# Revit family: BC_Hitachi_CH-Box-6.0-10.0_LOD400
name_source: partatom
category: Equipement de génie climatique
revit_build: Autodesk Revit 2016 (Build: 20150220_1215(x64)
units: mm (PartAtom-declared; Revit-internal decimal feet)

## family parameters
Basée sur le plan de construction = Non
Cote de connecteur circulaire = Utiliser le diamètre
Couper avec des vides une fois chargée = Non
Numéro OmniClass = 23.75.50.00
Partagée = Non
Point de calcul de pièce = Non
Titre OmniClass = Energy Treatment
Toujours verticalement = Oui
Type d'élément = Normal

## types (2) — shared parameters
Color = Neutral white (4.56Y8.85/0.38)
Description = Energy recovery box
Electrical Box = 63 mm
Fabricant = HITACHI
Frequency = 50 Hz
Gas HP distance = 20 mm  [stored 0.0656168 ft]
Gas High pressure Height = 94 mm
Gas low pressure Height = 40 mm
Input = 20 W
Mass = 7.00 kg
Modèle = Indoor unit CH Box CH-N2
Nominal Voltage = 240 V
Number of Poles = 1
Operation and service space = Oui
Overall Depth = 191 mm  [stored 0.62664 ft]
Overall Height = 301 mm
Overall Width = 214 mm  [stored 0.7021 ft]
Power Supply = 240 V
Refrigerant = R410A
Refrigerant Gas pipe Height = 111 mm
Refrigerant Gas pipe distance = 25 mm  [stored 0.082021 ft]

## per-type parameters (varying)
| type | High Pressure Gas Diameter | Left connector depth | Low Pressure Gas Diameter | Operation space | Product Code | Refrigerant Gas pipe diameter | Right connector depth |
| CH 10.0 N | 20 mm  [stored 0.0656168 ft] | 89 mm  [stored 0.291995 ft] | 20 mm  [stored 0.0656168 ft] | 400 mm  [stored 1.31234 ft] | 60291931 | 20 mm  [stored 0.0656168 ft] | 96 mm  [stored 0.314961 ft] |
| CH 6.0 N | 18 mm | 82 mm | 18 mm | 300 mm | 60291930 | 18 mm | 89 mm  [stored 0.291995 ft] |

note: column(s) folded — value = type name in every type: Commentaires du type

note: [stored X ft] marks values corroborated as IEEE doubles in the binary element streams (Revit-internal decimal feet)

## geometry (parser evidence)
native form markers: Blend x2
no freeform markers — native parametric forms only
